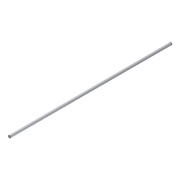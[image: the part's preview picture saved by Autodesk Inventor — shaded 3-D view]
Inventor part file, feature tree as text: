
AUTODESK INVENTOR PART (.ipt)
format: ipt  version: 2012 (Build 160160000, 160)  size: 62,464 bytes
history: native  units: in
note: dims shown in document units (in); Inventor stores cm internally (conversion verified against a paired STEP export)
features: extrude x1, plane x1, sketch x1, other x1
ambient origin geometry x8: Origin, YZ Plane, XZ Plane, XY Plane, X Axis, Y Axis, Z Axis, Center Point
bodies: Solid1 (feature_tree)
feature tree (4):
  extrude  "Extrusion1"  Depth=16.0in TaperAngle=0.0deg
  plane  "Work Plane1"
  sketch  "Sketch1"  dims[d0=0.25in d1=16.0in d2=0.0in d3=90.0deg]
  other  "Work Axis1"
